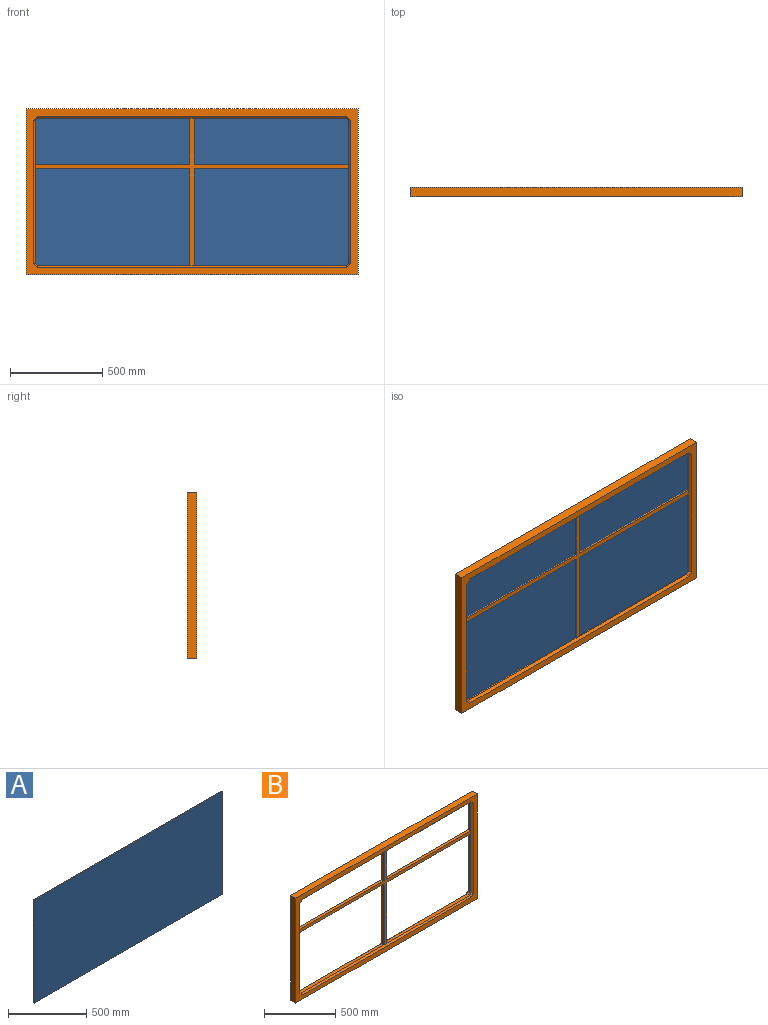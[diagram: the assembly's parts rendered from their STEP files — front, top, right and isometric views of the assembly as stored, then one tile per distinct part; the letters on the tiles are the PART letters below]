
ASSEMBLY  parts=2 mates=1
PART A: 6 faces, bbox 1700x10x800 mm
  f0: plane 800x10mm, normal (1,0,0), area 8000mm2, adj f1,f3,f4,f5
  f1: plane 1700x10mm, normal (0,0,1), area 17000mm2, adj f0,f2,f4,f5
  f2: plane 800x10mm, normal (-1,0,0), area 8000mm2, adj f1,f3,f4,f5
  f3: plane 1700x10mm, normal (0,0,-1), area 17000mm2, adj f0,f2,f4,f5
  f4: plane 1700x800mm, normal (0,-1,0), area 1360000mm2, adj f0,f1,f2,f3
  f5: plane 1700x800mm, normal (0,1,0), area 1360000mm2, adj f0,f1,f2,f3
PART B: 44 faces, bbox 1800x50x900 mm
  f0: plane 513x26mm, normal (1,0,0), area 13338mm2, adj f22,f23,f32,f40
  f1: plane 237x26mm, normal (-1,0,0), area 6162mm2, adj f20,f29,f30,f42
  f2: plane 249x26mm, normal (1,0,0), area 6474mm2, adj f8,f37,f39,f42
  f3: plane 249x26mm, normal (-1,0,0), area 6474mm2, adj f5,f37,f39,f41
  f4: plane 825x26mm, normal (0,0,1), area 21450mm2, adj f16,f23,f24,f38
  f5: plane 825x26mm, normal (0,0,-1), area 21450mm2, adj f3,f21,f31,f35
  f6: plane 1800x900mm, normal (0,1,0), area 200576mm2, adj f11,f12,f13,f14,f16,f17,f18,f20
  f7: plane 1800x900mm, normal (0,-1,0), area 200576mm2, adj f11,f12,f13,f14,f24,f25,f28,f29
  f8: plane 825x26mm, normal (0,0,-1), area 21450mm2, adj f2,f21,f30,f35
  f9: plane 513x26mm, normal (-1,0,0), area 13338mm2, adj f19,f20,f29,f43
  f10: plane 825x26mm, normal (0,0,1), area 21450mm2, adj f16,f19,f24,f36
  f11: plane 900x50mm, normal (1,0,0), area 45000mm2, adj f6,f7,f12,f14
  f12: plane 1800x50mm, normal (0,0,1), area 90000mm2, adj f6,f7,f11,f13
  f13: plane 900x50mm, normal (-1,0,0), area 45000mm2, adj f6,f7,f12,f14
  f14: plane 1800x50mm, normal (0,0,-1), area 90000mm2, adj f6,f7,f11,f13
  f15: plane 237x26mm, normal (1,0,0), area 6162mm2, adj f22,f31,f32,f41
  f16: plane 1676x12mm, normal (0,0.71,0.71), area 28442.7mm2, adj f4,f6,f10,f17,f18,f37
  f17: plane 24x24mm, normal (-0.58,0.58,0.58), area 374.1mm2, adj f6,f16,f19,f20
  f18: plane 24x24mm, normal (0.58,0.58,0.58), area 374.1mm2, adj f6,f16,f22,f23
  f19: plane 26x12mm, normal (-0.71,0,0.71), area 441.2mm2, adj f9,f10,f17,f25
  f20: plane 776x12mm, normal (-0.71,0.71,0), area 13169.2mm2, adj f1,f6,f9,f17,f26,f37
  f21: plane 1676x12mm, normal (0,0.71,-0.71), area 28442.7mm2, adj f5,f6,f8,f26,f27,f37
  f22: plane 776x12mm, normal (0.71,0.71,0), area 13169.2mm2, adj f0,f6,f15,f18,f27,f37
  f23: plane 26x12mm, normal (0.71,0,0.71), area 441.2mm2, adj f0,f4,f18,f28
  f24: plane 1676x12mm, normal (0,-0.71,0.71), area 28442.7mm2, adj f4,f7,f10,f25,f28,f39
  f25: plane 24x24mm, normal (-0.58,-0.58,0.58), area 374.1mm2, adj f7,f19,f24,f29
  f26: plane 24x24mm, normal (-0.58,0.58,-0.58), area 374.1mm2, adj f6,f20,f21,f30
  f27: plane 24x24mm, normal (0.58,0.58,-0.58), area 374.1mm2, adj f6,f21,f22,f31
  f28: plane 24x24mm, normal (0.58,-0.58,0.58), area 374.1mm2, adj f7,f23,f24,f32
  f29: plane 776x12mm, normal (-0.71,-0.71,0), area 13169.2mm2, adj f1,f7,f9,f25,f33,f39
  f30: plane 26x12mm, normal (-0.71,0,-0.71), area 441.2mm2, adj f1,f8,f26,f33
  f31: plane 26x12mm, normal (0.71,0,-0.71), area 441.2mm2, adj f5,f15,f27,f34
  f32: plane 776x12mm, normal (0.71,-0.71,0), area 13169.2mm2, adj f0,f7,f15,f28,f34,f39
  f33: plane 24x24mm, normal (-0.58,-0.58,-0.58), area 374.1mm2, adj f7,f29,f30,f35
  f34: plane 24x24mm, normal (0.58,-0.58,-0.58), area 374.1mm2, adj f7,f31,f32,f35
  f35: plane 1676x12mm, normal (0,-0.71,-0.71), area 28442.7mm2, adj f5,f7,f8,f33,f34,f39
  f36: plane 525x26mm, normal (1,0,0), area 13650mm2, adj f10,f37,f39,f43
  f37: plane 1700x800mm, normal (0,1,0), area 64324mm2, adj f2,f3,f16,f20,f21,f22,f36,f38
  f38: plane 525x26mm, normal (-1,0,0), area 13650mm2, adj f4,f37,f39,f40
  f39: plane 1700x800mm, normal (0,-1,0), area 64324mm2, adj f2,f3,f24,f29,f32,f35,f36,f38
  f40: plane 837x26mm, normal (0,0,-1), area 21762mm2, adj f0,f37,f38,f39
  f41: plane 837x26mm, normal (0,0,1), area 21762mm2, adj f3,f15,f37,f39
  f42: plane 837x26mm, normal (0,0,1), area 21762mm2, adj f1,f2,f37,f39
  f43: plane 837x26mm, normal (0,0,-1), area 21762mm2, adj f9,f36,f37,f39
PLACE A t=(0,-20,0)mm
PLACE B at identity
MATE fastened A.f0 <-> B.f1  axis (1,0,0) through (850,-25,400)mm
